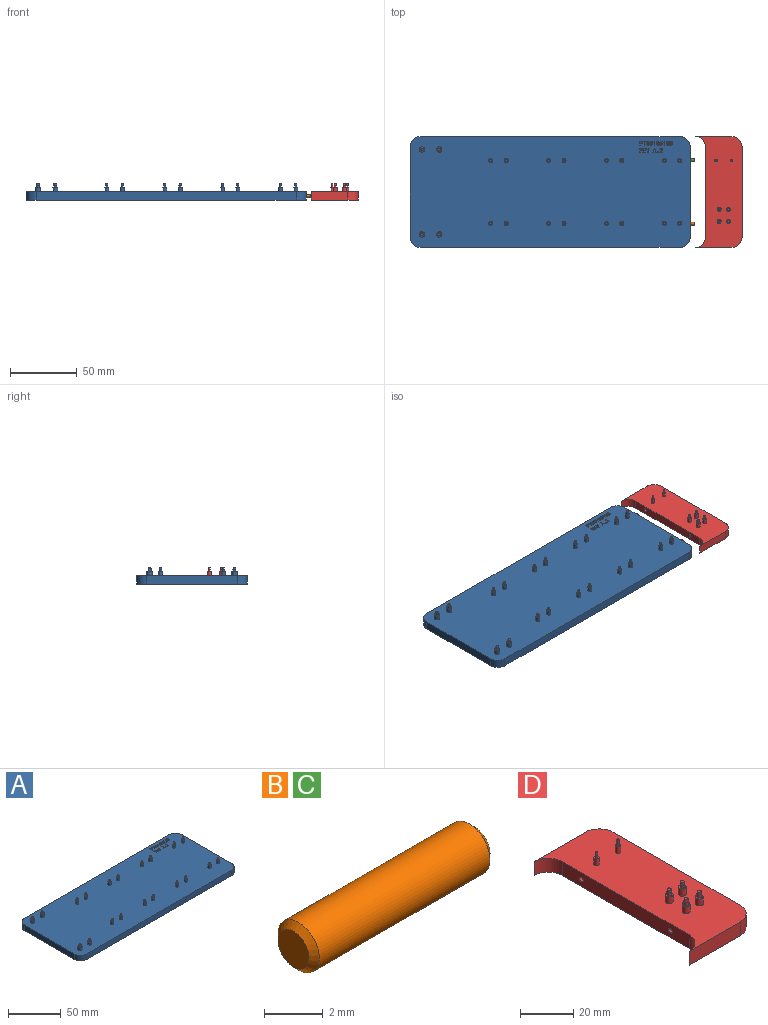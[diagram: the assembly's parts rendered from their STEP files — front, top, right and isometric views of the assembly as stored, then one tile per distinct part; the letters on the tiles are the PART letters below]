
ASSEMBLY  parts=4 mates=4
PART A: 356 faces, bbox 209.9x83.1x12.5 mm
  f0: plane 209.69x82.87mm, normal (0,0,1), area 17068.9mm2, adj f1,f2,f3,f4,f6,f8,f10,f12
  f1: plane 194.28x6.35mm, normal (0,1,0), area 1233.7mm2, adj f0,f5,f86,f89
  f2: plane 67.46x6.35mm, normal (-1,0,0), area 428.4mm2, adj f0,f5,f86,f87
  f3: plane 194.28x6.35mm, normal (0,-1,0), area 1233.7mm2, adj f0,f5,f87,f88
  f4: plane 67.46x6.35mm, normal (1,0,0), area 418.6mm2, adj f0,f5,f88,f89,f354,f355
  f5: plane 209.52x82.7mm, normal (0,0,-1), area 17277.3mm2, adj f1,f2,f3,f4,f86,f87,f88,f89
  f6: cylinder r=2mm len=4mm, axis (0,0,-1), area 39.9mm2, adj f0,f7
  f7: plane 4x4mm, normal (0,0,1), area 8.6mm2, adj f6,f46
  f8: cylinder r=2mm len=4mm, axis (0,0,-1), area 39.9mm2, adj f0,f9
  f9: plane 4x4mm, normal (0,0,1), area 8.6mm2, adj f8,f48
  f10: cylinder r=2mm len=4mm, axis (0,0,-1), area 39.9mm2, adj f0,f11
  f11: plane 4x4mm, normal (0,0,1), area 8.6mm2, adj f10,f50
  f12: cylinder r=2mm len=4mm, axis (0,0,-1), area 39.9mm2, adj f0,f13
  f13: plane 4x4mm, normal (0,0,1), area 8.6mm2, adj f12,f52
  f14: cylinder r=1.5mm len=3.18mm, axis (0,0,-1), area 29.9mm2, adj f0,f15
  f15: plane 3x3mm, normal (0,0,1), area 5mm2, adj f14,f54
  f16: cylinder r=1.5mm len=3.18mm, axis (0,0,-1), area 29.9mm2, adj f0,f17
  f17: plane 3x3mm, normal (0,0,1), area 5mm2, adj f16,f56
  f18: cylinder r=1.5mm len=3.18mm, axis (0,0,-1), area 29.9mm2, adj f0,f19
  f19: plane 3x3mm, normal (0,0,1), area 5mm2, adj f18,f58
  f20: cylinder r=1.5mm len=3.18mm, axis (0,0,-1), area 29.9mm2, adj f0,f21
  f21: plane 3x3mm, normal (0,0,1), area 5mm2, adj f20,f60
  f22: cylinder r=1.5mm len=3.18mm, axis (0,0,-1), area 29.9mm2, adj f0,f23
  f23: plane 3x3mm, normal (0,0,1), area 5mm2, adj f22,f62
  f24: cylinder r=1.5mm len=3.18mm, axis (0,0,-1), area 29.9mm2, adj f0,f25
  f25: plane 3x3mm, normal (0,0,1), area 5mm2, adj f24,f64
  f26: cylinder r=1.5mm len=3.18mm, axis (0,0,-1), area 29.9mm2, adj f0,f27
  f27: plane 3x3mm, normal (0,0,1), area 5mm2, adj f26,f66
  f28: cylinder r=1.5mm len=3.18mm, axis (0,0,-1), area 29.9mm2, adj f0,f29
  f29: plane 3x3mm, normal (0,0,1), area 5mm2, adj f28,f68
  f30: cylinder r=1.5mm len=3.18mm, axis (0,0,-1), area 29.9mm2, adj f0,f31
  f31: plane 3x3mm, normal (0,0,1), area 5mm2, adj f30,f70
  f32: cylinder r=1.5mm len=3.18mm, axis (0,0,-1), area 29.9mm2, adj f0,f33
  f33: plane 3x3mm, normal (0,0,1), area 5mm2, adj f32,f72
  f34: cylinder r=1.5mm len=3.18mm, axis (0,0,-1), area 29.9mm2, adj f0,f35
  f35: plane 3x3mm, normal (0,0,1), area 5mm2, adj f34,f74
  f36: cylinder r=1.5mm len=3.18mm, axis (0,0,-1), area 29.9mm2, adj f0,f37
  f37: plane 3x3mm, normal (0,0,1), area 5mm2, adj f36,f76
  f38: cylinder r=1.5mm len=3.18mm, axis (0,0,-1), area 29.9mm2, adj f0,f39
  f39: plane 3x3mm, normal (0,0,1), area 5mm2, adj f38,f78
  f40: cylinder r=1.5mm len=3.18mm, axis (0,0,-1), area 29.9mm2, adj f0,f41
  f41: plane 3x3mm, normal (0,0,1), area 5mm2, adj f40,f80
  f42: cylinder r=1.5mm len=3.18mm, axis (0,0,-1), area 29.9mm2, adj f0,f43
  f43: plane 3x3mm, normal (0,0,1), area 5mm2, adj f42,f82
  f44: cylinder r=1.5mm len=3.18mm, axis (0,0,-1), area 29.9mm2, adj f0,f45
  f45: plane 3x3mm, normal (0,0,1), area 5mm2, adj f44,f84
  f46: cylinder r=1.12mm len=2.46mm, axis (0,0,-1), area 17.4mm2, adj f7,f109
  f47: plane 0.05x0.05mm, normal (0,0,1), area 0mm2, adj f109
  f48: cylinder r=1.12mm len=2.25mm, axis (0,0,-1), area 10.2mm2, adj f9,f108
  f49: plane 2.1x2.1mm, normal (0,0,1), area 3.5mm2, adj f108
  f50: cylinder r=1.12mm len=2.25mm, axis (0,0,-1), area 10.2mm2, adj f11,f107
  f51: plane 2.1x2.1mm, normal (0,0,1), area 3.5mm2, adj f107
  f52: cylinder r=1.12mm len=2.25mm, axis (0,0,-1), area 10.2mm2, adj f13,f106
  f53: plane 2.1x2.1mm, normal (0,0,1), area 3.5mm2, adj f106
  f54: cylinder r=0.81mm len=1.63mm, axis (0,0,-1), area 7.4mm2, adj f15,f105
  f55: plane 1.47x1.47mm, normal (0,0,1), area 1.7mm2, adj f105
  f56: cylinder r=0.81mm len=1.63mm, axis (0,0,-1), area 7.4mm2, adj f17,f104
  f57: plane 1.47x1.47mm, normal (0,0,1), area 1.7mm2, adj f104
  f58: cylinder r=0.81mm len=1.63mm, axis (0,0,-1), area 7.4mm2, adj f19,f102
  f59: plane 1.47x1.47mm, normal (0,0,1), area 1.7mm2, adj f102
  f60: cylinder r=0.81mm len=1.63mm, axis (0,0,-1), area 7.4mm2, adj f21,f103
  f61: plane 1.47x1.47mm, normal (0,0,1), area 1.7mm2, adj f103
  f62: cylinder r=0.81mm len=1.63mm, axis (0,0,-1), area 7.4mm2, adj f23,f101
  f63: plane 1.47x1.47mm, normal (0,0,1), area 1.7mm2, adj f101
  f64: cylinder r=0.81mm len=1.63mm, axis (0,0,-1), area 7.4mm2, adj f25,f99
  f65: plane 1.47x1.47mm, normal (0,0,1), area 1.7mm2, adj f99
  f66: cylinder r=0.81mm len=1.63mm, axis (0,0,-1), area 7.4mm2, adj f27,f98
  f67: plane 1.47x1.47mm, normal (0,0,1), area 1.7mm2, adj f98
  f68: cylinder r=0.81mm len=1.63mm, axis (0,0,-1), area 7.4mm2, adj f29,f100
  f69: plane 1.47x1.47mm, normal (0,0,1), area 1.7mm2, adj f100
  f70: cylinder r=0.81mm len=1.63mm, axis (0,0,-1), area 7.4mm2, adj f31,f94
  f71: plane 1.47x1.47mm, normal (0,0,1), area 1.7mm2, adj f94
  f72: cylinder r=0.81mm len=1.63mm, axis (0,0,-1), area 7.4mm2, adj f33,f97
  f73: plane 1.47x1.47mm, normal (0,0,1), area 1.7mm2, adj f97
  f74: cylinder r=0.81mm len=1.63mm, axis (0,0,-1), area 7.4mm2, adj f35,f96
  f75: plane 1.47x1.47mm, normal (0,0,1), area 1.7mm2, adj f96
  f76: cylinder r=0.81mm len=1.63mm, axis (0,0,-1), area 7.4mm2, adj f37,f95
  f77: plane 1.47x1.47mm, normal (0,0,1), area 1.7mm2, adj f95
  f78: cylinder r=0.81mm len=1.63mm, axis (0,0,-1), area 7.4mm2, adj f39,f93
  f79: plane 1.47x1.47mm, normal (0,0,1), area 1.7mm2, adj f93
  f80: cylinder r=0.81mm len=1.63mm, axis (0,0,-1), area 7.4mm2, adj f41,f92
  f81: plane 1.47x1.47mm, normal (0,0,1), area 1.7mm2, adj f92
  f82: cylinder r=0.81mm len=1.63mm, axis (0,0,-1), area 7.4mm2, adj f43,f91
  f83: plane 1.47x1.47mm, normal (0,0,1), area 1.7mm2, adj f91
  f84: cylinder r=0.81mm len=1.63mm, axis (0,0,-1), area 7.4mm2, adj f45,f90
  f85: plane 1.47x1.47mm, normal (0,0,1), area 1.7mm2, adj f90
  f86: cylinder r=7.62mm len=7.62mm, axis (0,0,1), area 76mm2, adj f0,f1,f2,f5
  f87: cylinder r=7.62mm len=7.62mm, axis (0,0,-1), area 76mm2, adj f0,f2,f3,f5
  f88: cylinder r=7.62mm len=7.62mm, axis (0,0,1), area 76mm2, adj f0,f3,f4,f5
  f89: cylinder r=7.62mm len=7.62mm, axis (0,0,-1), area 76mm2, adj f0,f1,f4,f5
  f90: cone r=0.81mm half-angle=4deg, axis (0,0,-1), area 5.4mm2, adj f84,f85
  f91: cone r=0.81mm half-angle=4deg, axis (0,0,-1), area 5.4mm2, adj f82,f83
  f92: cone r=0.81mm half-angle=4deg, axis (0,0,-1), area 5.4mm2, adj f80,f81
  f93: cone r=0.81mm half-angle=4deg, axis (0,0,-1), area 5.4mm2, adj f78,f79
  f94: cone r=0.81mm half-angle=4deg, axis (0,0,-1), area 5.4mm2, adj f70,f71
  f95: cone r=0.81mm half-angle=4deg, axis (0,0,-1), area 5.4mm2, adj f76,f77
  f96: cone r=0.81mm half-angle=4deg, axis (0,0,-1), area 5.4mm2, adj f74,f75
  f97: cone r=0.81mm half-angle=4deg, axis (0,0,-1), area 5.4mm2, adj f72,f73
  f98: cone r=0.81mm half-angle=4deg, axis (0,0,-1), area 5.4mm2, adj f66,f67
  f99: cone r=0.81mm half-angle=4deg, axis (0,0,-1), area 5.4mm2, adj f64,f65
  f100: cone r=0.81mm half-angle=4deg, axis (0,0,-1), area 5.4mm2, adj f68,f69
  f101: cone r=0.81mm half-angle=4deg, axis (0,0,-1), area 5.4mm2, adj f62,f63
  f102: cone r=0.81mm half-angle=4deg, axis (0,0,-1), area 5.4mm2, adj f58,f59
  f103: cone r=0.81mm half-angle=4deg, axis (0,0,-1), area 5.4mm2, adj f60,f61
  f104: cone r=0.81mm half-angle=4deg, axis (0,0,-1), area 5.4mm2, adj f56,f57
  f105: cone r=0.81mm half-angle=4deg, axis (0,0,-1), area 5.4mm2, adj f54,f55
  f106: cone r=1.12mm half-angle=4deg, axis (0,0,-1), area 7.5mm2, adj f52,f53
  f107: cone r=1.12mm half-angle=4deg, axis (0,0,-1), area 7.5mm2, adj f50,f51
  f108: cone r=1.12mm half-angle=4deg, axis (0,0,-1), area 7.5mm2, adj f48,f49
  f109: cone r=0.03mm half-angle=86deg, axis (0,0,-1), area 4mm2, adj f46,f47
  f110: plane 1x0.38mm, normal (0,0.98,0.17), area 0.2mm2, adj f0,f111,f117,f118
  f111: plane 2.81x1mm, normal (-0.98,0,0.17), area 2.7mm2, adj f0,f110,f112,f114,f118
  f112: plane 1.02x0.95mm, normal (0,0.98,0.17), area 0.8mm2, adj f0,f111,f113,f114
  f113: plane 0.95x0.33mm, normal (-0.98,0,0.17), area 0.2mm2, adj f0,f112,f114
  f114: plane 2.08x1mm, normal (0,-0.98,0.17), area 1.8mm2, adj f0,f111,f112,f113,f115,f116,f117,f118
  f115: plane 0.95x0.33mm, normal (0.98,0,0.17), area 0.2mm2, adj f0,f114,f116
  f116: plane 1.02x0.95mm, normal (0,0.98,0.17), area 0.8mm2, adj f0,f114,f115,f117
  f117: plane 2.81x1mm, normal (0.98,0,0.17), area 2.7mm2, adj f0,f110,f114,f116,f118
  f118: plane 2.62x0.03mm, normal (0,0,1), area 0.1mm2, adj f110,f111,f114,f117
  f119: plane 0.91x0.55mm, normal (0,0.98,0.17), area 0.4mm2, adj f0,f123,f125,f126,f132
  f120: bspline ~1.2x0.9mm, area 1.2mm2, adj f121,f124,f128,f129,f133,f348
  f121: plane 0.92x0.57mm, normal (0,0.98,0.17), area 0.5mm2, adj f120,f125,f129,f348
  f122: plane 2.62x0.03mm, normal (0,0,1), area 0.1mm2, adj f125,f129,f130,f131
  f123: plane 0.91x0.51mm, normal (0,-0.98,0.17), area 0.4mm2, adj f119,f125,f132,f348
  f124: bspline ~1.2x0.62mm, area 0.6mm2, adj f120,f126,f132,f133,f348
  f125: plane 2.81x1mm, normal (-0.98,0,0.17), area 2.5mm2, adj f0,f119,f121,f122,f123,f129,f131,f348
  f126: bspline ~1x0.82mm, area 0.8mm2, adj f0,f119,f124,f127,f132,f133
  f127: bspline ~1.2x0.7mm, area 0.7mm2, adj f0,f126,f128,f133
  f128: bspline ~1.2x1.05mm, area 1.5mm2, adj f0,f120,f127,f129,f133
  f129: plane 1x0.82mm, normal (0,-0.98,0.17), area 0.7mm2, adj f0,f120,f121,f122,f125,f128,f130
  f130: plane 2.97x1mm, normal (0.98,0,0.17), area 2.8mm2, adj f0,f122,f129,f131
  f131: plane 1x0.38mm, normal (0,0.98,0.17), area 0.2mm2, adj f0,f122,f125,f130
  f132: bspline ~1.2x0.71mm, area 0.6mm2, adj f119,f123,f124,f126,f348
  f133: plane 1.63x0.85mm, normal (0,0,1), area 0mm2, adj f120,f124,f126,f127,f128
  f134: bspline ~1.2x0.63mm, area 0.6mm2, adj f136,f140,f144,f150
  f135: bspline ~1.2x0.62mm, area 0.6mm2, adj f138,f142,f147,f150
  f136: bspline ~1.2x1.02mm, area 1mm2, adj f134,f137,f144,f149,f150
  f137: bspline ~1.2x1.02mm, area 1mm2, adj f136,f142,f145,f149,f150
  f138: bspline ~1.2x1.02mm, area 1mm2, adj f135,f139,f141,f147,f150
  f139: plane 1.83x0.24mm, normal (0,0,1), area 0mm2, adj f138,f141,f147,f148
  f140: bspline ~1.2x0.62mm, area 0.6mm2, adj f134,f141,f143,f148,f150
  f141: bspline ~1.2x1.02mm, area 1mm2, adj f138,f139,f140,f148,f150
  f142: bspline ~1.2x0.63mm, area 0.6mm2, adj f135,f137,f145,f146,f150
  f143: bspline ~1.2x0.71mm, area 0.7mm2, adj f0,f140,f144,f148
  f144: bspline ~1.53x1.2mm, area 1.9mm2, adj f0,f134,f136,f143,f145,f149
  f145: bspline ~1.2x1.14mm, area 1.1mm2, adj f0,f137,f142,f144,f146,f149
  f146: bspline ~1.2x0.71mm, area 0.7mm2, adj f0,f142,f145,f147
  f147: bspline ~1.53x1.2mm, area 1.9mm2, adj f0,f135,f138,f139,f146,f148
  f148: bspline ~1.2x1.14mm, area 1.1mm2, adj f0,f139,f140,f141,f143,f147
  f149: plane 1.79x0.22mm, normal (0,0,1), area 0mm2, adj f136,f137,f144,f145
  f150: plane 2.6x1.32mm, normal (0,0,1), area 2.4mm2, adj f134,f135,f136,f137,f138,f140,f141,f142
  f151: bspline ~1.2x0.63mm, area 0.6mm2, adj f153,f157,f161,f167
  f152: bspline ~1.2x0.62mm, area 0.6mm2, adj f155,f159,f164,f167
  f153: bspline ~1.2x1.02mm, area 1mm2, adj f151,f154,f161,f166,f167
  f154: bspline ~1.2x1.02mm, area 1mm2, adj f153,f159,f162,f166,f167
  f155: bspline ~1.2x1.02mm, area 1mm2, adj f152,f156,f158,f164,f167
  f156: plane 1.83x0.24mm, normal (0,0,1), area 0mm2, adj f155,f158,f164,f165
  f157: bspline ~1.2x0.62mm, area 0.6mm2, adj f151,f158,f160,f165,f167
  f158: bspline ~1.2x1.02mm, area 1mm2, adj f155,f156,f157,f165,f167
  f159: bspline ~1.2x0.63mm, area 0.6mm2, adj f152,f154,f162,f163,f167
  f160: bspline ~1.2x0.71mm, area 0.7mm2, adj f0,f157,f161,f165
  f161: bspline ~1.53x1.2mm, area 1.9mm2, adj f0,f151,f153,f160,f162,f166
  f162: bspline ~1.2x1.14mm, area 1.1mm2, adj f0,f154,f159,f161,f163,f166
  f163: bspline ~1.2x0.71mm, area 0.7mm2, adj f0,f159,f162,f164
  f164: bspline ~1.53x1.2mm, area 1.9mm2, adj f0,f152,f155,f156,f163,f165
  f165: bspline ~1.2x1.14mm, area 1.1mm2, adj f0,f156,f157,f158,f160,f164
  f166: plane 1.79x0.22mm, normal (0,0,1), area 0mm2, adj f153,f154,f161,f162
  f167: plane 2.6x1.32mm, normal (0,0,1), area 2.4mm2, adj f151,f152,f153,f154,f155,f157,f158,f159
  f168: bspline ~1.2x0.63mm, area 0.6mm2, adj f170,f174,f178,f184
  f169: bspline ~1.2x0.62mm, area 0.6mm2, adj f172,f176,f181,f184
  f170: bspline ~1.2x1.02mm, area 1mm2, adj f168,f171,f178,f183,f184
  f171: bspline ~1.2x1.02mm, area 1mm2, adj f170,f176,f179,f183,f184
  f172: bspline ~1.2x1.02mm, area 1mm2, adj f169,f173,f175,f181,f184
  f173: plane 1.83x0.24mm, normal (0,0,1), area 0mm2, adj f172,f175,f181,f182
  f174: bspline ~1.2x0.62mm, area 0.6mm2, adj f168,f175,f177,f182,f184
  f175: bspline ~1.2x1.02mm, area 1mm2, adj f172,f173,f174,f182,f184
  f176: bspline ~1.2x0.63mm, area 0.6mm2, adj f169,f171,f179,f180,f184
  f177: bspline ~1.2x0.71mm, area 0.7mm2, adj f0,f174,f178,f182
  f178: bspline ~1.53x1.2mm, area 1.9mm2, adj f0,f168,f170,f177,f179,f183
  f179: bspline ~1.2x1.14mm, area 1.1mm2, adj f0,f171,f176,f178,f180,f183
  f180: bspline ~1.2x0.71mm, area 0.7mm2, adj f0,f176,f179,f181
  f181: bspline ~1.53x1.2mm, area 1.9mm2, adj f0,f169,f172,f173,f180,f182
  f182: bspline ~1.2x1.14mm, area 1.1mm2, adj f0,f173,f174,f175,f177,f181
  f183: plane 1.79x0.22mm, normal (0,0,1), area 0mm2, adj f170,f171,f178,f179
  f184: plane 2.6x1.32mm, normal (0,0,1), area 2.4mm2, adj f168,f169,f170,f171,f172,f174,f175,f176
  f185: plane 1.06x0.61mm, normal (0,-0.98,0.17), area 0.2mm2, adj f0,f190,f193,f194,f198
  f186: plane 1.24x0.95mm, normal (0,-0.98,0.17), area 1mm2, adj f187,f188,f197,f349
  f187: plane 1.08x1mm, normal (0.94,0.29,0.17), area 1mm2, adj f186,f189,f193,f197,f198,f349
  f188: plane 1.18x1.01mm, normal (-0.94,0.29,0.17), area 1.1mm2, adj f186,f190,f194,f197,f199,f349
  f189: plane 1.43x0.47mm, normal (0,0,1), area 0mm2, adj f187,f191,f192,f193,f197
  f190: bspline ~1.23x1.2mm, area 0.5mm2, adj f185,f188,f194,f198,f349
  f191: plane 1.1x1mm, normal (0.94,0.3,0.17), area 1mm2, adj f0,f189,f192,f197
  f192: plane 1x0.39mm, normal (0,0.98,0.17), area 0.2mm2, adj f0,f189,f191,f193
  f193: plane 3.05x1.15mm, normal (-0.94,-0.31,0.17), area 2.9mm2, adj f0,f185,f187,f189,f192,f198
  f194: plane 3.07x1.17mm, normal (0.94,-0.31,0.17), area 2.9mm2, adj f0,f185,f188,f190,f195,f199
  f195: plane 1x0.39mm, normal (0,0.98,0.17), area 0.2mm2, adj f0,f194,f196,f199
  f196: plane 1.1x1mm, normal (-0.94,0.3,0.17), area 1mm2, adj f0,f195,f197,f199
  f197: plane 1.26x1mm, normal (0,0.98,0.17), area 1.1mm2, adj f0,f186,f187,f188,f189,f191,f196,f199
  f198: bspline ~1.31x1.2mm, area 0.6mm2, adj f185,f187,f190,f193,f349
  f199: plane 1.45x0.48mm, normal (0,0,1), area 0mm2, adj f188,f194,f195,f196,f197
  f200: bspline ~1.2x0.65mm, area 0.5mm2, adj f201,f202,f203,f209,f211,f213,f219
  f201: plane 0.91x0.49mm, normal (0,-0.98,0.17), area 0.4mm2, adj f200,f210,f211,f219
  f202: plane 1.4x1mm, normal (0.85,0.49,0.17), area 1.4mm2, adj f0,f200,f203,f206,f211,f212
  f203: plane 1.49x1.12mm, normal (-0.84,-0.51,0.17), area 1.5mm2, adj f0,f200,f202,f206,f212,f213
  f204: bspline ~1x0.63mm, area 0.6mm2, adj f205,f208,f214,f215,f218,f219
  f205: plane 0.92x0.49mm, normal (0,0.98,0.17), area 0.4mm2, adj f204,f210,f215,f219
  f206: plane 1.17x0.71mm, normal (0,0,1), area 0mm2, adj f202,f203,f212
  f207: plane 2.62x0.03mm, normal (0,0,1), area 0.1mm2, adj f210,f215,f216,f217
  f208: bspline ~1.2x0.58mm, area 0.5mm2, adj f204,f209,f218,f219
  f209: bspline ~1.2x0.59mm, area 0.5mm2, adj f200,f208,f213,f218,f219
  f210: plane 2.81x1mm, normal (-0.98,0,0.17), area 2.5mm2, adj f0,f201,f205,f207,f211,f215,f217,f219
  f211: plane 0.98x0.75mm, normal (0,0.98,0.17), area 0.6mm2, adj f0,f200,f201,f202,f210
  f212: plane 1x0.45mm, normal (0,0.98,0.17), area 0.2mm2, adj f0,f202,f203,f206
  f213: bspline ~1.2x0.88mm, area 1mm2, adj f0,f200,f203,f209,f214,f218
  f214: bspline ~1.2x1.06mm, area 1.4mm2, adj f0,f204,f213,f215,f218
  f215: plane 1x0.73mm, normal (0,-0.98,0.17), area 0.6mm2, adj f0,f204,f205,f207,f210,f214,f216
  f216: plane 2.97x1mm, normal (0.98,0,0.17), area 2.8mm2, adj f0,f207,f215,f217
  f217: plane 1x0.38mm, normal (0,0.98,0.17), area 0.2mm2, adj f0,f207,f210,f216
  f218: plane 1.29x0.64mm, normal (0,0,1), area 0mm2, adj f204,f208,f209,f213,f214
  f219: plane 1.14x1.05mm, normal (0,0,1), area 1mm2, adj f200,f201,f204,f205,f208,f209,f210
  f220: bspline ~1.2x0.63mm, area 0.6mm2, adj f222,f226,f230,f236
  f221: bspline ~1.2x0.62mm, area 0.6mm2, adj f224,f228,f233,f236
  f222: bspline ~1.2x1.02mm, area 1mm2, adj f220,f223,f230,f235,f236
  f223: bspline ~1.2x1.02mm, area 1mm2, adj f222,f228,f231,f235,f236
  f224: bspline ~1.2x1.02mm, area 1mm2, adj f221,f225,f227,f233,f236
  f225: plane 1.83x0.24mm, normal (0,0,1), area 0mm2, adj f224,f227,f233,f234
  f226: bspline ~1.2x0.62mm, area 0.6mm2, adj f220,f227,f229,f234,f236
  f227: bspline ~1.2x1.02mm, area 1mm2, adj f224,f225,f226,f234,f236
  f228: bspline ~1.2x0.63mm, area 0.6mm2, adj f221,f223,f231,f232,f236
  f229: bspline ~1.2x0.71mm, area 0.7mm2, adj f0,f226,f230,f234
  f230: bspline ~1.53x1.2mm, area 1.9mm2, adj f0,f220,f222,f229,f231,f235
  f231: bspline ~1.2x1.14mm, area 1.1mm2, adj f0,f223,f228,f230,f232,f235
  f232: bspline ~1.2x0.71mm, area 0.7mm2, adj f0,f228,f231,f233
  f233: bspline ~1.53x1.2mm, area 1.9mm2, adj f0,f221,f224,f225,f232,f234
  f234: bspline ~1.2x1.14mm, area 1.1mm2, adj f0,f225,f226,f227,f229,f233
  f235: plane 1.79x0.22mm, normal (0,0,1), area 0mm2, adj f222,f223,f230,f231
  f236: plane 2.6x1.32mm, normal (0,0,1), area 2.4mm2, adj f220,f221,f222,f223,f224,f226,f227,f228
  f237: bspline ~1.2x0.86mm, area 0.7mm2, adj f0,f248,f249,f250,f251
  f238: bspline ~1.2x0.79mm, area 0.8mm2, adj f0,f244,f245,f253,f254
  f239: plane 0.18x0.1mm, normal (0,0,1), area 0mm2, adj f240,f243,f254,f255
  f240: plane 1.85x1mm, normal (0,0.98,0.17), area 1.6mm2, adj f0,f239,f241,f242,f243,f255
  f241: plane 0.96x0.34mm, normal (-0.98,0,0.17), area 0.2mm2, adj f0,f240,f242
  f242: plane 1.57x0.96mm, normal (0,-0.98,0.17), area 1.4mm2, adj f0,f240,f241,f243
  f243: plane 1x0.25mm, normal (-0.98,0,0.17), area 0.1mm2, adj f0,f239,f240,f242,f244,f254
  f244: plane 0.91x0.73mm, normal (-0.72,0.67,0.17), area 0.8mm2, adj f0,f238,f243,f245,f254
  f245: bspline ~1.2x0.85mm, area 0.9mm2, adj f0,f238,f244,f246,f253
  f246: bspline ~1.2x0.5mm, area 0.5mm2, adj f0,f245,f247,f253,f256
  f247: bspline ~1.2x0.58mm, area 0.6mm2, adj f0,f246,f248,f256
  f248: bspline ~1.2x0.62mm, area 0.6mm2, adj f0,f237,f247,f251,f256
  f249: plane 1.23x0.57mm, normal (0.75,0.64,0.17), area 0.1mm2, adj f0,f237,f250
  f250: bspline ~1.2x0.79mm, area 0.7mm2, adj f0,f237,f249,f251
  f251: bspline ~1.2x0.5mm, area 0.4mm2, adj f0,f237,f248,f250,f252,f256
  f252: bspline ~1.2x0.51mm, area 0.5mm2, adj f0,f251,f253,f256
  f253: bspline ~1.2x0.58mm, area 0.5mm2, adj f0,f238,f245,f246,f252,f256
  f254: plane 1x0.84mm, normal (0.72,-0.67,0.17), area 0.9mm2, adj f0,f238,f239,f243,f244,f255
  f255: plane 1x0.32mm, normal (0.98,0,0.17), area 0.2mm2, adj f0,f239,f240,f254
  f256: plane 0.93x0.28mm, normal (0,0,1), area 0mm2, adj f246,f247,f248,f251,f252,f253
  f257: bspline ~1.2x0.34mm, area 0.4mm2, adj f0,f258,f260,f261
  f258: bspline ~1.2x0.34mm, area 0.4mm2, adj f0,f257,f259,f261
  f259: bspline ~1.2x0.34mm, area 0.4mm2, adj f0,f258,f260,f261
  f260: bspline ~1.2x0.34mm, area 0.4mm2, adj f0,f257,f259,f261
  f261: plane 0.4x0.34mm, normal (0,0,1), area 0.1mm2, adj f257,f258,f259,f260
  f262: bspline ~1.52x1.2mm, area 0.8mm2, adj f0,f263,f267,f269,f270
  f263: plane 1.95x1.01mm, normal (-0.94,-0.3,0.17), area 1.9mm2, adj f0,f262,f264,f268,f269
  f264: plane 1.72x0.57mm, normal (0,0,1), area 0mm2, adj f263,f268,f269
  f265: plane 1x0.41mm, normal (0,-0.98,0.17), area 0.2mm2, adj f0,f266,f271,f272
  f266: plane 1.93x1mm, normal (0.94,-0.3,0.17), area 1.9mm2, adj f0,f265,f267,f272
  f267: bspline ~1.53x1.2mm, area 0.9mm2, adj f0,f262,f266,f270,f271,f272
  f268: plane 1x0.4mm, normal (0,-0.98,0.17), area 0.2mm2, adj f0,f263,f264,f269
  f269: plane 3.13x1.25mm, normal (0.93,0.31,0.17), area 2.9mm2, adj f0,f262,f263,f264,f268,f270
  f270: plane 1.2x0.77mm, normal (0,0.98,0.17), area 0.2mm2, adj f0,f262,f267,f269,f271
  f271: plane 2.99x1.11mm, normal (-0.93,0.31,0.17), area 2.9mm2, adj f0,f265,f267,f270,f272
  f272: plane 1.78x0.59mm, normal (0,0,1), area 0mm2, adj f265,f266,f267,f271
  f273: plane 2.64x1mm, normal (-0.98,0,0.17), area 2.4mm2, adj f0,f274,f276,f277,f279,f280,f282,f284
  f274: plane 1.71x1mm, normal (0,0.98,0.17), area 1.5mm2, adj f0,f273,f275,f276,f283,f284
  f275: plane 0.95x0.33mm, normal (-0.98,0,0.17), area 0.2mm2, adj f0,f274,f276
  f276: plane 1.5x0.95mm, normal (0,-0.98,0.17), area 1.3mm2, adj f0,f273,f274,f275
  f277: plane 1.42x0.93mm, normal (0,0.98,0.17), area 1.2mm2, adj f0,f273,f278,f279
  f278: plane 0.93x0.33mm, normal (-0.98,0,0.17), area 0.2mm2, adj f0,f277,f279
  f279: plane 1.42x0.93mm, normal (0,-0.98,0.17), area 1.2mm2, adj f0,f273,f277,f278
  f280: plane 1.5x0.95mm, normal (0,0.98,0.17), area 1.3mm2, adj f0,f273,f281,f282
  f281: plane 0.95x0.33mm, normal (-0.98,0,0.17), area 0.2mm2, adj f0,f280,f282
  f282: plane 1.71x1mm, normal (0,-0.98,0.17), area 1.5mm2, adj f0,f273,f280,f281,f283,f284
  f283: plane 2.97x1mm, normal (0.98,0,0.17), area 2.8mm2, adj f0,f274,f282,f284
  f284: plane 2.62x0.03mm, normal (0,0,1), area 0.1mm2, adj f273,f274,f282,f283
  f285: bspline ~1.2x0.66mm, area 0.4mm2, adj f0,f288,f289,f297,f298
  f286: bspline ~1.2x0.79mm, area 0.7mm2, adj f0,f303,f304,f305,f306
  f287: plane 1.03x0.42mm, normal (0,0,1), area 0mm2, adj f302,f303,f306,f307,f308
  f288: plane 1.17x0.37mm, normal (-0.98,0,0.17), area 0.1mm2, adj f0,f285,f298,f302,f308
  f289: bspline ~1.2x0.47mm, area 0.5mm2, adj f0,f285,f290,f297,f309
  f290: bspline ~1.2x0.54mm, area 0.5mm2, adj f0,f289,f291,f309
  f291: bspline ~1.2x0.65mm, area 0.6mm2, adj f0,f290,f292,f295,f309
  f292: bspline ~1.2x0.89mm, area 0.8mm2, adj f0,f291,f293,f294
  f293: plane 1.23x0.58mm, normal (0.79,0.58,0.17), area 0.1mm2, adj f0,f292,f294
  f294: bspline ~1.2x0.82mm, area 0.7mm2, adj f0,f292,f293,f295
  f295: bspline ~1.2x0.51mm, area 0.4mm2, adj f0,f291,f294,f296,f309
  f296: bspline ~1.2x0.49mm, area 0.4mm2, adj f0,f295,f297,f309
  f297: bspline ~1.2x0.57mm, area 0.5mm2, adj f0,f285,f289,f296,f298,f309
  f298: bspline ~1.2x0.64mm, area 0.5mm2, adj f0,f285,f288,f297,f299,f302
  f299: plane 0.87x0.27mm, normal (0,-0.98,0.17), area 0.2mm2, adj f0,f298,f300,f301
  f300: plane 0.87x0.31mm, normal (0.98,0,0.17), area 0.1mm2, adj f0,f299,f301
  f301: plane 0.87x0.27mm, normal (0,0.98,0.17), area 0.2mm2, adj f0,f299,f300,f302
  f302: bspline ~1.2x0.99mm, area 1mm2, adj f0,f287,f288,f298,f301,f303,f308
  f303: bspline ~1.2x0.93mm, area 1.2mm2, adj f0,f286,f287,f302,f304,f306
  f304: bspline ~1.2x0.88mm, area 0.6mm2, adj f0,f286,f303,f305
  f305: plane 1.29x0.73mm, normal (0.98,0,0.17), area 0.2mm2, adj f0,f286,f304
  f306: bspline ~1.2x0.81mm, area 0.8mm2, adj f0,f286,f287,f303,f307
  f307: bspline ~1.2x0.65mm, area 0.7mm2, adj f0,f287,f306,f308
  f308: bspline ~1.2x0.92mm, area 1mm2, adj f0,f287,f288,f302,f307
  f309: plane 0.84x0.35mm, normal (0,0,1), area 0mm2, adj f289,f290,f291,f295,f296,f297
  f310: bspline ~1.2x0.77mm, area 0.4mm2, adj f0,f313,f314,f316,f317
  f311: plane 1x0.36mm, normal (0,0.98,0.17), area 0.2mm2, adj f0,f312,f318,f319
  f312: plane 3.25x1.28mm, normal (-0.98,0,0.17), area 2.8mm2, adj f0,f311,f313,f317,f319
  f313: plane 0.97x0.33mm, normal (0,-0.98,0.17), area 0.2mm2, adj f0,f310,f312,f314,f317
  f314: plane 0.98x0.91mm, normal (0.61,-0.78,0.17), area 0.7mm2, adj f0,f310,f313,f315,f316
  f315: plane 0.89x0.25mm, normal (0.77,0.61,0.17), area 0.1mm2, adj f0,f314,f316
  f316: plane 0.94x0.41mm, normal (-0.63,0.76,0.17), area 0.3mm2, adj f0,f310,f314,f315
  f317: bspline ~1.22x1.2mm, area 0.9mm2, adj f0,f310,f312,f313,f318,f319
  f318: plane 1.86x1mm, normal (0.98,0,0.17), area 1.8mm2, adj f0,f311,f317,f319
  f319: plane 2.32x0.28mm, normal (0,0,1), area 0mm2, adj f311,f312,f317,f318
  f320: plane 1.4x0.99mm, normal (0.98,-0.08,0.17), area 1.3mm2, adj f0,f321,f330,f333
  f321: plane 1.06x0.33mm, normal (0.53,0.83,0.17), area 0.1mm2, adj f0,f320,f329,f330,f334
  f322: bspline ~1.2x0.85mm, area 0.6mm2, adj f0,f323,f324,f325,f336
  f323: plane 1.06x0.52mm, normal (0.98,0,0.17), area 0.2mm2, adj f0,f322,f324
  f324: bspline ~1.2x0.72mm, area 0.6mm2, adj f0,f322,f323,f325
  f325: bspline ~1.2x0.79mm, area 0.7mm2, adj f0,f322,f324,f326,f336
  f326: bspline ~1.2x0.74mm, area 0.7mm2, adj f0,f325,f327,f336,f337
  f327: bspline ~1.2x0.64mm, area 0.6mm2, adj f0,f326,f328,f337
  f328: bspline ~1.2x0.69mm, area 0.7mm2, adj f0,f327,f329,f335,f337
  f329: bspline ~1.2x0.68mm, area 0.4mm2, adj f0,f321,f328,f330,f334,f335
  f330: plane 1.2x1mm, normal (-0.98,0.09,0.17), area 1mm2, adj f0,f320,f321,f329,f331,f333
  f331: plane 1.24x0.96mm, normal (0,0.98,0.17), area 1mm2, adj f0,f330,f332,f333
  f332: plane 0.96x0.34mm, normal (-0.98,0,0.17), area 0.2mm2, adj f0,f331,f333
  f333: plane 1.4x0.99mm, normal (0,-0.98,0.17), area 1.2mm2, adj f0,f320,f330,f331,f332
  f334: bspline ~1.2x0.51mm, area 0.4mm2, adj f0,f321,f329,f335
  f335: bspline ~1.2x0.91mm, area 1.2mm2, adj f0,f328,f329,f334,f336,f337
  f336: bspline ~1.2x0.9mm, area 1.2mm2, adj f0,f322,f325,f326,f335,f337
  f337: plane 1.21x0.42mm, normal (0,0,1), area 0mm2, adj f326,f327,f328,f335,f336
  f338: bspline ~1.2x0.77mm, area 0.4mm2, adj f0,f341,f342,f344,f345
  f339: plane 1x0.36mm, normal (0,0.98,0.17), area 0.2mm2, adj f0,f340,f346,f347
  f340: plane 3.25x1.28mm, normal (-0.98,0,0.17), area 2.8mm2, adj f0,f339,f341,f345,f347
  f341: plane 0.97x0.33mm, normal (0,-0.98,0.17), area 0.2mm2, adj f0,f338,f340,f342,f345
  f342: plane 0.98x0.91mm, normal (0.61,-0.78,0.17), area 0.7mm2, adj f0,f338,f341,f343,f344
  f343: plane 0.89x0.25mm, normal (0.77,0.61,0.17), area 0.1mm2, adj f0,f342,f344
  f344: plane 0.94x0.41mm, normal (-0.63,0.76,0.17), area 0.3mm2, adj f0,f338,f342,f343
  f345: bspline ~1.22x1.2mm, area 0.9mm2, adj f0,f338,f340,f341,f346,f347
  f346: plane 1.86x1mm, normal (0.98,0,0.17), area 1.8mm2, adj f0,f339,f345,f347
  f347: plane 2.32x0.28mm, normal (0,0,1), area 0mm2, adj f339,f340,f345,f346
  f348: plane 1.22x1.14mm, normal (0,0,1), area 1.2mm2, adj f120,f121,f123,f124,f125,f132
  f349: plane 1.35x0.81mm, normal (0,0,1), area 0.5mm2, adj f186,f187,f188,f190,f198
  f350: cylinder r=1mm len=5.25mm, axis (1,0,0), area 33mm2, adj f351,f354
  f351: plane 2x2mm, normal (1,0,0), area 3.1mm2, adj f350
  f352: cylinder r=1mm len=5.25mm, axis (1,0,0), area 33mm2, adj f353,f355
  f353: plane 2x2mm, normal (1,0,0), area 3.1mm2, adj f352
  f354: cone r=1mm half-angle=45deg, axis (1,0,0), area 2.5mm2, adj f4,f350
  f355: cone r=1mm half-angle=45deg, axis (1,0,0), area 2.5mm2, adj f4,f352
PART B: 5 faces, bbox 8.8x2x2 mm
  f0: cylinder r=1mm len=8.25mm, axis (-1,0,0), area 51.8mm2, adj f3,f4
  f1: plane 1.5x1.5mm, normal (1,0,0), area 1.8mm2, adj f4
  f2: plane 1.5x1.5mm, normal (-1,0,0), area 1.8mm2, adj f3
  f3: cone r=1mm half-angle=45deg, axis (1,0,0), area 1.9mm2, adj f0,f2
  f4: cone r=0.75mm half-angle=45deg, axis (-1,0,0), area 1.9mm2, adj f0,f1
PART C: same geometry as B
PART D: 50 faces, bbox 34.8x82.7x12.1 mm
  f0: plane 82.7x34.82mm, normal (0,0,1), area 2214.9mm2, adj f1,f2,f3,f4,f5,f7,f8,f9
  f1: plane 67.46x6.35mm, normal (-1,0,0), area 422.1mm2, adj f0,f2,f6,f8,f40,f42
  f2: cylinder r=7.62mm len=7.62mm, axis (0,0,-1), area 76mm2, adj f0,f1,f3,f6
  f3: plane 27.2x6.35mm, normal (0,-1,0), area 172.7mm2, adj f0,f2,f4,f6
  f4: cylinder r=7.62mm len=7.62mm, axis (0,0,-1), area 76mm2, adj f0,f3,f5,f6
  f5: plane 67.46x6.35mm, normal (1,0,0), area 418.6mm2, adj f0,f4,f6,f7,f48,f49
  f6: plane 82.7x34.82mm, normal (0,0,-1), area 2249.4mm2, adj f1,f2,f3,f4,f5,f7,f8,f9
  f7: cylinder r=7.62mm len=7.62mm, axis (0,0,-1), area 76mm2, adj f0,f5,f6,f9
  f8: cylinder r=7.62mm len=7.62mm, axis (0,0,-1), area 76mm2, adj f0,f1,f6,f9
  f9: plane 27.2x6.35mm, normal (0,1,0), area 172.7mm2, adj f0,f6,f7,f8
  f10: plane 2x2mm, normal (0,0,1), area 2.3mm2, adj f11,f23
  f11: cylinder r=1mm len=3.18mm, axis (0,0,-1), area 19.9mm2, adj f0,f10
  f12: plane 2x2mm, normal (0,0,1), area 2.3mm2, adj f13,f25
  f13: cylinder r=1mm len=3.18mm, axis (0,0,-1), area 19.9mm2, adj f0,f12
  f14: plane 3x3mm, normal (0,0,1), area 4.9mm2, adj f15,f27
  f15: cylinder r=1.5mm len=3.18mm, axis (0,0,-1), area 29.9mm2, adj f0,f14
  f16: plane 3x3mm, normal (0,0,1), area 4.9mm2, adj f17,f29
  f17: cylinder r=1.5mm len=3.18mm, axis (0,0,-1), area 29.9mm2, adj f0,f16
  f18: plane 3x3mm, normal (0,0,1), area 4.9mm2, adj f19,f31
  f19: cylinder r=1.5mm len=3.18mm, axis (0,0,-1), area 29.9mm2, adj f0,f18
  f20: plane 3x3mm, normal (0,0,1), area 4.9mm2, adj f21,f33
  f21: cylinder r=1.5mm len=3.18mm, axis (0,0,-1), area 29.9mm2, adj f0,f20
  f22: plane 0.9x0.9mm, normal (0,0,1), area 0.6mm2, adj f39
  f23: cylinder r=0.53mm len=1.44mm, axis (0,0,-1), area 4.8mm2, adj f10,f39
  f24: plane 0.9x0.9mm, normal (0,0,1), area 0.6mm2, adj f38
  f25: cylinder r=0.53mm len=1.44mm, axis (0,0,-1), area 4.8mm2, adj f12,f38
  f26: plane 1.5x1.5mm, normal (0,0,1), area 1.8mm2, adj f37
  f27: cylinder r=0.82mm len=1.65mm, axis (0,0,-1), area 7.5mm2, adj f14,f37
  f28: plane 1.5x1.5mm, normal (0,0,1), area 1.8mm2, adj f36
  f29: cylinder r=0.82mm len=1.65mm, axis (0,0,-1), area 7.5mm2, adj f16,f36
  f30: plane 1.5x1.5mm, normal (0,0,1), area 1.8mm2, adj f35
  f31: cylinder r=0.82mm len=1.65mm, axis (0,0,-1), area 7.5mm2, adj f18,f35
  f32: plane 1.5x1.5mm, normal (0,0,1), area 1.8mm2, adj f34
  f33: cylinder r=0.82mm len=1.65mm, axis (0,0,-1), area 7.5mm2, adj f20,f34
  f34: cone r=0.75mm half-angle=4deg, axis (0,0,-1), area 5.4mm2, adj f32,f33
  f35: cone r=0.75mm half-angle=4deg, axis (0,0,-1), area 5.4mm2, adj f30,f31
  f36: cone r=0.75mm half-angle=4deg, axis (0,0,-1), area 5.4mm2, adj f28,f29
  f37: cone r=0.75mm half-angle=4deg, axis (0,0,-1), area 5.4mm2, adj f26,f27
  f38: cone r=0.45mm half-angle=4deg, axis (0,0,-1), area 3.4mm2, adj f24,f25
  f39: cone r=0.45mm half-angle=4deg, axis (0,0,-1), area 3.4mm2, adj f22,f23
  f40: cylinder r=1mm len=5.5mm, axis (-1,0,0), area 34.6mm2, adj f1,f41
  f41: plane 2x2mm, normal (-1,0,0), area 3.1mm2, adj f40
  f42: cylinder r=1mm len=5.5mm, axis (-1,0,0), area 34.6mm2, adj f1,f43
  f43: plane 2x2mm, normal (-1,0,0), area 3.1mm2, adj f42
  f44: cylinder r=1mm len=5.25mm, axis (1,0,0), area 33mm2, adj f45,f48
  f45: plane 2x2mm, normal (1,0,0), area 3.1mm2, adj f44
  f46: cylinder r=1mm len=5.25mm, axis (1,0,0), area 33mm2, adj f47,f49
  f47: plane 2x2mm, normal (1,0,0), area 3.1mm2, adj f46
  f48: cone r=1mm half-angle=45deg, axis (1,0,0), area 2.5mm2, adj f5,f44
  f49: cone r=1mm half-angle=45deg, axis (1,0,0), area 2.5mm2, adj f5,f46
PLACE A t=(-60.39,15.37,18.89)mm
PLACE B t=(-93.09,15.37,18.89)mm
PLACE C t=(-93.09,62.83,18.89)mm
PLACE D t=(-48.91,15.37,18.89)mm
MATE slider C.f0 <-> D.f42  axis (-1,0,0) through (152.12,80.45,22.06)mm
MATE slider B.f0 <-> D.f40  axis (-1,0,0) through (152.12,32.99,22.06)mm
MATE fastened C.f0 <-> A.f350  axis (-1,0,0) through (143.62,80.45,22.06)mm
MATE fastened B.f0 <-> A.f352  axis (-1,0,0) through (143.62,32.99,22.06)mm
